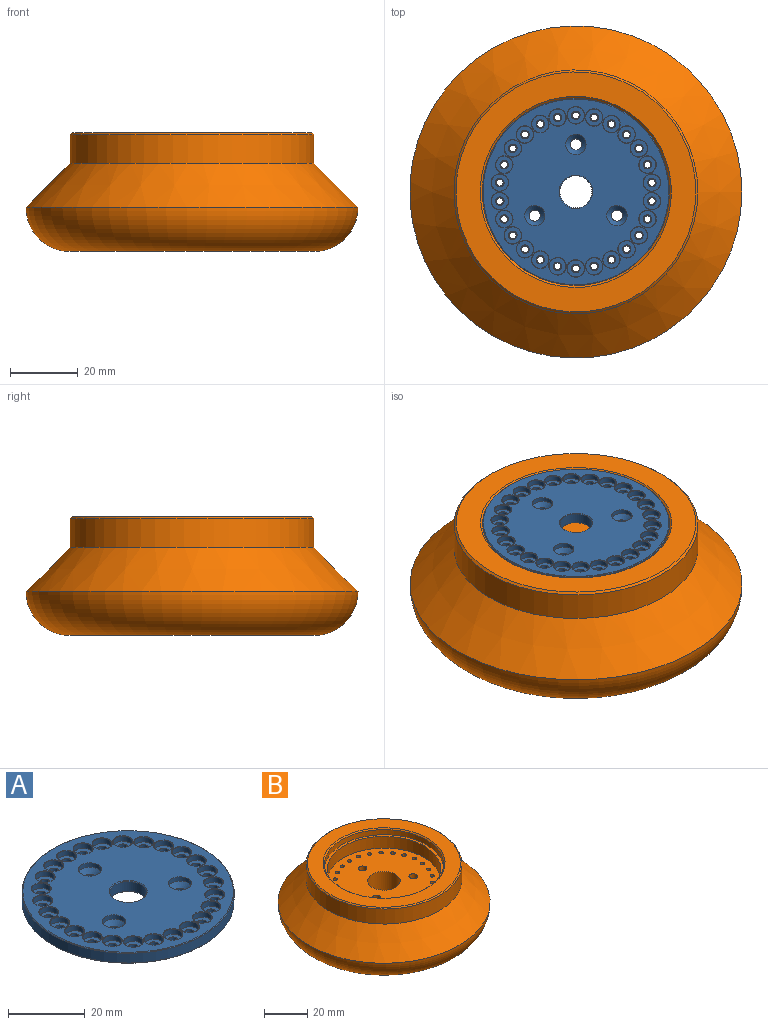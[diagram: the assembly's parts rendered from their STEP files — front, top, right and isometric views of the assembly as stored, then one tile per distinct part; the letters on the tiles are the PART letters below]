
ASSEMBLY  parts=2 mates=1
PART A: 130 faces, bbox 55.2x55.2x10.1 mm
  f0: cylinder r=4.75mm len=9.5mm, axis (0,0,-1), area 92.5mm2, adj f108,f109
  f1: cylinder r=27.6mm len=55.2mm, axis (0,0,-1), area 537.6mm2, adj f110,f111
  f2: plane 54.8x54.8mm, normal (0,0,1), area 1644.6mm2, adj f7,f11,f15,f19,f23,f27,f31,f35
  f3: plane 54.8x54.8mm, normal (0,0,-1), area 1963.1mm2, adj f4,f8,f12,f16,f20,f24,f28,f32
  f4: cylinder r=1.25mm len=2.5mm, axis (0,0,1), area 14.1mm2, adj f3,f5
  f5: plane 5x5mm, normal (0,0,1), area 14.7mm2, adj f4,f6
  f6: cylinder r=2.5mm len=5mm, axis (0,0,1), area 25.1mm2, adj f5,f7
  f7: cone r=2.5mm half-angle=45deg, axis (0,0,1), area 2.3mm2, adj f2,f6
  f8: cylinder r=1.25mm len=2.5mm, axis (0,0,1), area 14.1mm2, adj f3,f9
  f9: plane 5x5mm, normal (0,0,1), area 14.7mm2, adj f8,f10
  f10: cylinder r=2.5mm len=5mm, axis (0,0,1), area 25.1mm2, adj f9,f11
  f11: cone r=2.5mm half-angle=45deg, axis (0,0,1), area 2.3mm2, adj f2,f10
  f12: cylinder r=1.25mm len=2.5mm, axis (0,0,1), area 14.1mm2, adj f3,f13
  f13: plane 5x5mm, normal (0,0,1), area 14.7mm2, adj f12,f14
  f14: cylinder r=2.5mm len=5mm, axis (0,0,1), area 25.1mm2, adj f13,f15
  f15: cone r=2.5mm half-angle=45deg, axis (0,0,1), area 2.3mm2, adj f2,f14
  f16: cylinder r=1.25mm len=2.5mm, axis (0,0,1), area 14.1mm2, adj f3,f17
  f17: plane 5x5mm, normal (0,0,1), area 14.7mm2, adj f16,f18
  f18: cylinder r=2.5mm len=5mm, axis (0,0,1), area 25.1mm2, adj f17,f19
  f19: cone r=2.5mm half-angle=45deg, axis (0,0,1), area 2.3mm2, adj f2,f18
  f20: cylinder r=1.25mm len=2.5mm, axis (0,0,1), area 14.1mm2, adj f3,f21
  f21: plane 5x5mm, normal (0,0,1), area 14.7mm2, adj f20,f22
  f22: cylinder r=2.5mm len=5mm, axis (0,0,1), area 25.1mm2, adj f21,f23
  f23: cone r=2.5mm half-angle=45deg, axis (0,0,1), area 2.3mm2, adj f2,f22
  f24: cylinder r=1.25mm len=2.5mm, axis (0,0,1), area 14.1mm2, adj f3,f25
  f25: plane 5x5mm, normal (0,0,1), area 14.7mm2, adj f24,f26
  f26: cylinder r=2.5mm len=5mm, axis (0,0,1), area 25.1mm2, adj f25,f27
  f27: cone r=2.5mm half-angle=45deg, axis (0,0,1), area 2.3mm2, adj f2,f26
  f28: cylinder r=1.25mm len=2.5mm, axis (0,0,1), area 14.1mm2, adj f3,f29
  f29: plane 5x5mm, normal (0,0,1), area 14.7mm2, adj f28,f30
  f30: cylinder r=2.5mm len=5mm, axis (0,0,1), area 25.1mm2, adj f29,f31
  f31: cone r=2.5mm half-angle=45deg, axis (0,0,1), area 2.3mm2, adj f2,f30
  f32: cylinder r=1.25mm len=2.5mm, axis (0,0,1), area 14.1mm2, adj f3,f33
  f33: plane 5x5mm, normal (0,0,1), area 14.7mm2, adj f32,f34
  f34: cylinder r=2.5mm len=5mm, axis (0,0,1), area 25.1mm2, adj f33,f35
  f35: cone r=2.5mm half-angle=45deg, axis (0,0,1), area 2.3mm2, adj f2,f34
  f36: cylinder r=1.25mm len=2.5mm, axis (0,0,1), area 14.1mm2, adj f3,f37
  f37: plane 5x5mm, normal (0,0,1), area 14.7mm2, adj f36,f38
  f38: cylinder r=2.5mm len=5mm, axis (0,0,1), area 25.1mm2, adj f37,f39
  f39: cone r=2.5mm half-angle=45deg, axis (0,0,1), area 2.3mm2, adj f2,f38
  f40: cylinder r=1.25mm len=2.5mm, axis (0,0,1), area 14.1mm2, adj f3,f41
  f41: plane 5x5mm, normal (0,0,1), area 14.7mm2, adj f40,f42
  f42: cylinder r=2.5mm len=5mm, axis (0,0,1), area 25.1mm2, adj f41,f43
  f43: cone r=2.5mm half-angle=45deg, axis (0,0,1), area 2.3mm2, adj f2,f42
  f44: cylinder r=1.25mm len=2.5mm, axis (0,0,1), area 14.1mm2, adj f3,f45
  f45: plane 5x5mm, normal (0,0,1), area 14.7mm2, adj f44,f46
  f46: cylinder r=2.5mm len=5mm, axis (0,0,1), area 25.1mm2, adj f45,f47
  f47: cone r=2.5mm half-angle=45deg, axis (0,0,1), area 2.3mm2, adj f2,f46
  f48: cylinder r=1.25mm len=2.5mm, axis (0,0,1), area 14.1mm2, adj f3,f49
  f49: plane 5x5mm, normal (0,0,1), area 14.7mm2, adj f48,f50
  f50: cylinder r=2.5mm len=5mm, axis (0,0,1), area 25.1mm2, adj f49,f51
  f51: cone r=2.5mm half-angle=45deg, axis (0,0,1), area 2.3mm2, adj f2,f50
  f52: cylinder r=1.25mm len=2.5mm, axis (0,0,1), area 14.1mm2, adj f3,f53
  f53: plane 5x5mm, normal (0,0,1), area 14.7mm2, adj f52,f54
  f54: cylinder r=2.5mm len=5mm, axis (0,0,1), area 25.1mm2, adj f53,f55
  f55: cone r=2.5mm half-angle=45deg, axis (0,0,1), area 2.3mm2, adj f2,f54
  f56: cylinder r=1.25mm len=2.5mm, axis (0,0,1), area 14.1mm2, adj f3,f57
  f57: plane 5x5mm, normal (0,0,1), area 14.7mm2, adj f56,f58
  f58: cylinder r=2.5mm len=5mm, axis (0,0,1), area 25.1mm2, adj f57,f59
  f59: cone r=2.5mm half-angle=45deg, axis (0,0,1), area 2.3mm2, adj f2,f58
  f60: cylinder r=1.25mm len=2.5mm, axis (0,0,1), area 14.1mm2, adj f3,f61
  f61: plane 5x5mm, normal (0,0,1), area 14.7mm2, adj f60,f62
  f62: cylinder r=2.5mm len=5mm, axis (0,0,1), area 25.1mm2, adj f61,f63
  f63: cone r=2.5mm half-angle=45deg, axis (0,0,1), area 2.3mm2, adj f2,f62
  f64: cylinder r=1.25mm len=2.5mm, axis (0,0,1), area 14.1mm2, adj f3,f65
  f65: plane 5x5mm, normal (0,0,1), area 14.7mm2, adj f64,f66
  f66: cylinder r=2.5mm len=5mm, axis (0,0,1), area 25.1mm2, adj f65,f67
  f67: cone r=2.5mm half-angle=45deg, axis (0,0,1), area 2.3mm2, adj f2,f66
  f68: cylinder r=1.25mm len=2.5mm, axis (0,0,1), area 14.1mm2, adj f3,f69
  f69: plane 5x5mm, normal (0,0,1), area 14.7mm2, adj f68,f70
  f70: cylinder r=2.5mm len=5mm, axis (0,0,1), area 25.1mm2, adj f69,f71
  f71: cone r=2.5mm half-angle=45deg, axis (0,0,1), area 2.3mm2, adj f2,f70
  f72: cylinder r=1.25mm len=2.5mm, axis (0,0,1), area 14.1mm2, adj f3,f73
  f73: plane 5x5mm, normal (0,0,1), area 14.7mm2, adj f72,f74
  f74: cylinder r=2.5mm len=5mm, axis (0,0,1), area 25.1mm2, adj f73,f75
  f75: cone r=2.5mm half-angle=45deg, axis (0,0,1), area 2.3mm2, adj f2,f74
  f76: cylinder r=1.25mm len=2.5mm, axis (0,0,1), area 14.1mm2, adj f3,f77
  f77: plane 5x5mm, normal (0,0,1), area 14.7mm2, adj f76,f78
  f78: cylinder r=2.5mm len=5mm, axis (0,0,1), area 25.1mm2, adj f77,f79
  f79: cone r=2.5mm half-angle=45deg, axis (0,0,1), area 2.3mm2, adj f2,f78
  f80: cylinder r=1.25mm len=2.5mm, axis (0,0,1), area 14.1mm2, adj f3,f81
  f81: plane 5x5mm, normal (0,0,1), area 14.7mm2, adj f80,f82
  f82: cylinder r=2.5mm len=5mm, axis (0,0,1), area 25.1mm2, adj f81,f83
  f83: cone r=2.5mm half-angle=45deg, axis (0,0,1), area 2.3mm2, adj f2,f82
  f84: cylinder r=1.25mm len=2.5mm, axis (0,0,1), area 14.1mm2, adj f3,f85
  f85: plane 5x5mm, normal (0,0,1), area 14.7mm2, adj f84,f86
  f86: cylinder r=2.5mm len=5mm, axis (0,0,1), area 25.1mm2, adj f85,f87
  f87: cone r=2.5mm half-angle=45deg, axis (0,0,1), area 2.3mm2, adj f2,f86
  f88: cylinder r=1.25mm len=2.5mm, axis (0,0,1), area 14.1mm2, adj f3,f89
  f89: plane 5x5mm, normal (0,0,1), area 14.7mm2, adj f88,f90
  f90: cylinder r=2.5mm len=5mm, axis (0,0,1), area 25.1mm2, adj f89,f91
  f91: cone r=2.5mm half-angle=45deg, axis (0,0,1), area 2.3mm2, adj f2,f90
  f92: cylinder r=1.25mm len=2.5mm, axis (0,0,1), area 14.1mm2, adj f3,f93
  f93: plane 5x5mm, normal (0,0,1), area 14.7mm2, adj f92,f94
  f94: cylinder r=2.5mm len=5mm, axis (0,0,1), area 25.1mm2, adj f93,f95
  f95: cone r=2.5mm half-angle=45deg, axis (0,0,1), area 2.3mm2, adj f2,f94
  f96: cylinder r=1.25mm len=2.5mm, axis (0,0,1), area 14.1mm2, adj f3,f97
  f97: plane 5x5mm, normal (0,0,1), area 14.7mm2, adj f96,f98
  f98: cylinder r=2.5mm len=5mm, axis (0,0,1), area 25.1mm2, adj f97,f99
  f99: cone r=2.5mm half-angle=45deg, axis (0,0,1), area 2.3mm2, adj f2,f98
  f100: cylinder r=1.25mm len=2.5mm, axis (0,0,1), area 14.1mm2, adj f3,f101
  f101: plane 5x5mm, normal (0,0,1), area 14.7mm2, adj f100,f102
  f102: cylinder r=2.5mm len=5mm, axis (0,0,1), area 25.1mm2, adj f101,f103
  f103: cone r=2.5mm half-angle=45deg, axis (0,0,1), area 2.3mm2, adj f2,f102
  f104: cylinder r=1.25mm len=2.5mm, axis (0,0,1), area 14.1mm2, adj f3,f105
  f105: plane 5x5mm, normal (0,0,1), area 14.7mm2, adj f104,f106
  f106: cylinder r=2.5mm len=5mm, axis (0,0,1), area 25.1mm2, adj f105,f107
  f107: cone r=2.5mm half-angle=45deg, axis (0,0,1), area 2.3mm2, adj f2,f106
  f108: cone r=4.95mm half-angle=45deg, axis (0,0,-1), area 8.6mm2, adj f0,f3
  f109: cone r=4.75mm half-angle=45deg, axis (0,0,1), area 8.6mm2, adj f0,f2
  f110: cone r=27.6mm half-angle=45deg, axis (0,0,1), area 48.9mm2, adj f1,f3
  f111: cone r=27.4mm half-angle=45deg, axis (0,0,-1), area 48.9mm2, adj f1,f2
  f112: plane 6x6mm, normal (0,0,-1), area 19.7mm2, adj f113,f114
  f113: cylinder r=1.65mm len=7.4mm, axis (0,0,1), area 76.7mm2, adj f112,f117
  f114: cylinder r=3mm len=6mm, axis (0,0,1), area 96.1mm2, adj f112,f116
  f115: cylinder r=3mm len=6mm, axis (0,0,1), area 25.4mm2, adj f2,f117
  f116: cone r=4.5mm half-angle=45deg, axis (0,0,1), area 50mm2, adj f3,f114
  f117: cone r=1.65mm half-angle=45deg, axis (0,0,1), area 27.9mm2, adj f113,f115
  f118: plane 6x6mm, normal (0,0,-1), area 19.7mm2, adj f119,f120
  f119: cylinder r=1.65mm len=7.4mm, axis (0,0,1), area 76.7mm2, adj f118,f123
  f120: cylinder r=3mm len=6mm, axis (0,0,1), area 96.1mm2, adj f118,f122
  f121: cylinder r=3mm len=6mm, axis (0,0,1), area 25.4mm2, adj f2,f123
  f122: cone r=4.5mm half-angle=45deg, axis (0,0,1), area 50mm2, adj f3,f120
  f123: cone r=1.65mm half-angle=45deg, axis (0,0,1), area 27.9mm2, adj f119,f121
  f124: plane 6x6mm, normal (0,0,-1), area 19.7mm2, adj f125,f126
  f125: cylinder r=1.65mm len=7.4mm, axis (0,0,1), area 76.7mm2, adj f124,f129
  f126: cylinder r=3mm len=6mm, axis (0,0,1), area 96.1mm2, adj f124,f128
  f127: cylinder r=3mm len=6mm, axis (0,0,1), area 25.4mm2, adj f2,f129
  f128: cone r=4.5mm half-angle=45deg, axis (0,0,1), area 50mm2, adj f3,f126
  f129: cone r=1.65mm half-angle=45deg, axis (0,0,1), area 27.9mm2, adj f125,f127
PART B: 42 faces, bbox 106.1x106.1x35.1 mm
  f0: plane 50x50mm, normal (0,0,-1), area 1667.4mm2, adj f3,f4,f5,f6,f13,f16,f17,f18
  f1: cylinder r=36mm len=72mm, axis (0,0,1), area 1922.7mm2, adj f12,f14
  f2: plane 52.5x52.5mm, normal (0,0,1), area 1868.7mm2, adj f3,f4,f5,f6,f8,f16,f17,f18
  f3: cylinder r=2mm len=12mm, axis (0,0,1), area 150.8mm2, adj f0,f2
  f4: cylinder r=2mm len=12mm, axis (0,0,1), area 150.8mm2, adj f0,f2
  f5: cylinder r=2mm len=12mm, axis (0,0,1), area 150.8mm2, adj f0,f2
  f6: cylinder r=7.5mm len=15mm, axis (0,0,1), area 565.5mm2, adj f0,f2
  f7: plane 55.2x55.2mm, normal (0,0,1), area 228.4mm2, adj f8,f9
  f8: cylinder r=26.25mm len=52.5mm, axis (0,0,-1), area 1088.6mm2, adj f2,f7
  f9: cylinder r=27.6mm len=55.2mm, axis (0,0,-1), area 502.9mm2, adj f7,f15
  f10: plane 70.8x70.8mm, normal (0,0,1), area 1438.6mm2, adj f14,f15
  f11: torus R=36mm, axis (0,0,1), area 8151.1mm2, adj f12,f13
  f12: cone r=49mm half-angle=45deg, axis (0,0,-1), area 4909.4mm2, adj f1,f11
  f13: cylinder r=25mm len=50mm, axis (0,0,1), area 1088.3mm2, adj f0,f11
  f14: cone r=35.4mm half-angle=45deg, axis (0,0,-1), area 190.3mm2, adj f1,f10
  f15: cone r=27.6mm half-angle=45deg, axis (0,0,1), area 148.7mm2, adj f9,f10
  f16: cylinder r=1mm len=12mm, axis (0,0,1), area 75.4mm2, adj f0,f2
  f17: cylinder r=1mm len=12mm, axis (0,0,1), area 75.4mm2, adj f0,f2
  f18: cylinder r=1mm len=12mm, axis (0,0,1), area 75.4mm2, adj f0,f2
  f19: cylinder r=1mm len=12mm, axis (0,0,1), area 75.4mm2, adj f0,f2
  f20: cylinder r=1mm len=12mm, axis (0,0,1), area 75.4mm2, adj f0,f2
  f21: cylinder r=1mm len=12mm, axis (0,0,1), area 75.4mm2, adj f0,f2
  f22: cylinder r=1mm len=12mm, axis (0,0,1), area 75.4mm2, adj f0,f2
  f23: cylinder r=1mm len=12mm, axis (0,0,1), area 75.4mm2, adj f0,f2
  f24: cylinder r=1mm len=12mm, axis (0,0,1), area 75.4mm2, adj f0,f2
  f25: cylinder r=1mm len=12mm, axis (0,0,1), area 75.4mm2, adj f0,f2
  f26: cylinder r=1mm len=12mm, axis (0,0,1), area 75.4mm2, adj f0,f2
  f27: cylinder r=1mm len=12mm, axis (0,0,1), area 75.4mm2, adj f0,f2
  f28: cylinder r=1mm len=12mm, axis (0,0,1), area 75.4mm2, adj f0,f2
  f29: cylinder r=1mm len=12mm, axis (0,0,1), area 75.4mm2, adj f0,f2
  f30: cylinder r=1mm len=12mm, axis (0,0,1), area 75.4mm2, adj f0,f2
  f31: cylinder r=1mm len=12mm, axis (0,0,1), area 75.4mm2, adj f0,f2
  f32: cylinder r=1mm len=12mm, axis (0,0,1), area 75.4mm2, adj f0,f2
  f33: cylinder r=1mm len=12mm, axis (0,0,1), area 75.4mm2, adj f0,f2
  f34: cylinder r=1mm len=12mm, axis (0,0,1), area 75.4mm2, adj f0,f2
  f35: cylinder r=1mm len=12mm, axis (0,0,1), area 75.4mm2, adj f0,f2
  f36: cylinder r=1mm len=12mm, axis (0,0,1), area 75.4mm2, adj f0,f2
  f37: cylinder r=1mm len=12mm, axis (0,0,1), area 75.4mm2, adj f0,f2
  f38: cylinder r=1mm len=12mm, axis (0,0,1), area 75.4mm2, adj f0,f2
  f39: cylinder r=1mm len=12mm, axis (0,0,1), area 75.4mm2, adj f0,f2
  f40: cylinder r=1mm len=12mm, axis (0,0,1), area 75.4mm2, adj f0,f2
  f41: cylinder r=1mm len=12mm, axis (0,0,1), area 75.4mm2, adj f0,f2
PLACE A at identity fixed
PLACE B t=(0,0,-6.6)mm
MATE fastened A.f0 <-> B.f1  axis (0,0,1) through (0,0,-6.6)mm
